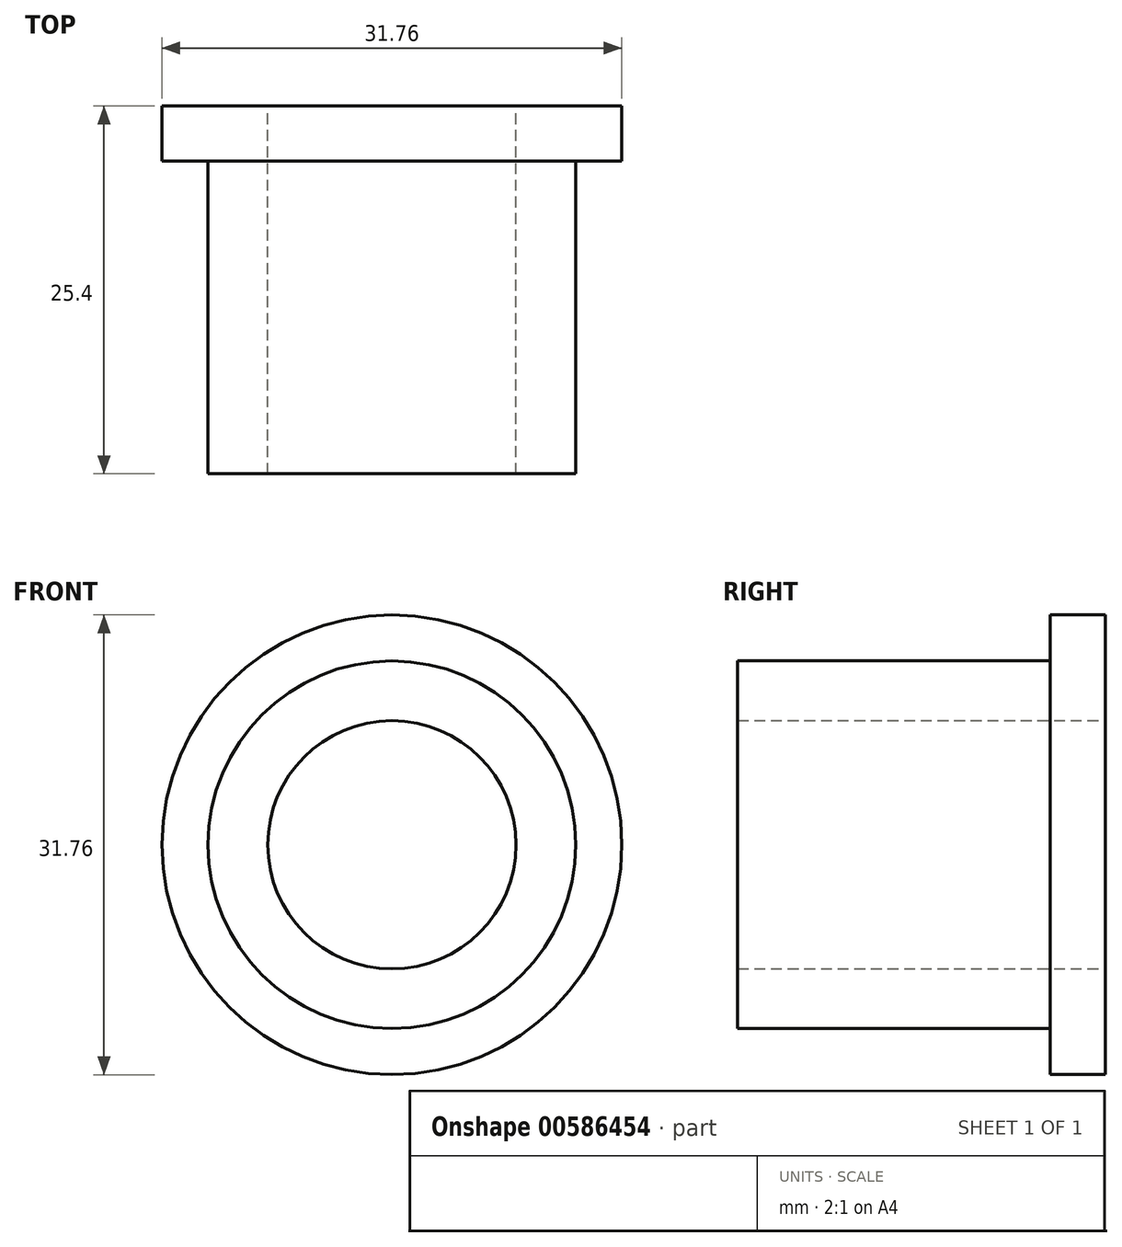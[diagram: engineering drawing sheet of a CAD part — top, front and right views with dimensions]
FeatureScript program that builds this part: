
annotation { "Feature Type Name" : "Feature", "Feature Type Description" : "" }
export const myFeature = defineFeature(function(context is Context, id is Id, definition is map)
    precondition{}
    {
        {
            var Q0;
            Q0=qCreatedBy(makeId("Front.planeOp"),FACE);
            var sketch = newSketch(context, id + "F0", { "sketchPlane" : qUnion([Q0])});
            skCircle(sketch, "E0", {"center": v(0, 0) * mm, "radius": 15.88 * mm});
            skCircle(sketch, "E1", {"center": v(0, 0) * mm, "radius": 8.57 * mm});
            skCircle(sketch, "E2", {"center": v(0, 0) * mm, "radius": 12.7 * mm});
            skSolve(sketch);
        }
        {
            var Q0;
            Q0=makeQuery(id+"F0.imprint","IMPRINT",FACE,{"disambiguationData":[TD([[makeQuery(id+"F0.imprint","IMPRINT",EDGE,{"derivedFrom":sQuery(id+"F0.wireOp",EDGE,"E1")}),-1.0]])]});
            extrude(context, id + "F1", {"entities" : qUnion([Q0]), "depth" : 25.4 * mm, "offsetDistance" : 25.4 * mm});
        }
        {
            var Q0;
            Q0=makeQuery(id+"F0.imprint","IMPRINT",FACE,{"disambiguationData":[TD([[makeQuery(id+"F0.imprint","IMPRINT",EDGE,{"derivedFrom":sQuery(id+"F0.wireOp",EDGE,"E0")}),1.0]])]});
            extrude(context, id + "F2", {"entities" : qUnion([Q0]), "operationType" : NewBodyOperationType.ADD, "depth" : 3.8 * mm, "offsetDistance" : 25.4 * mm});
        }
    });
